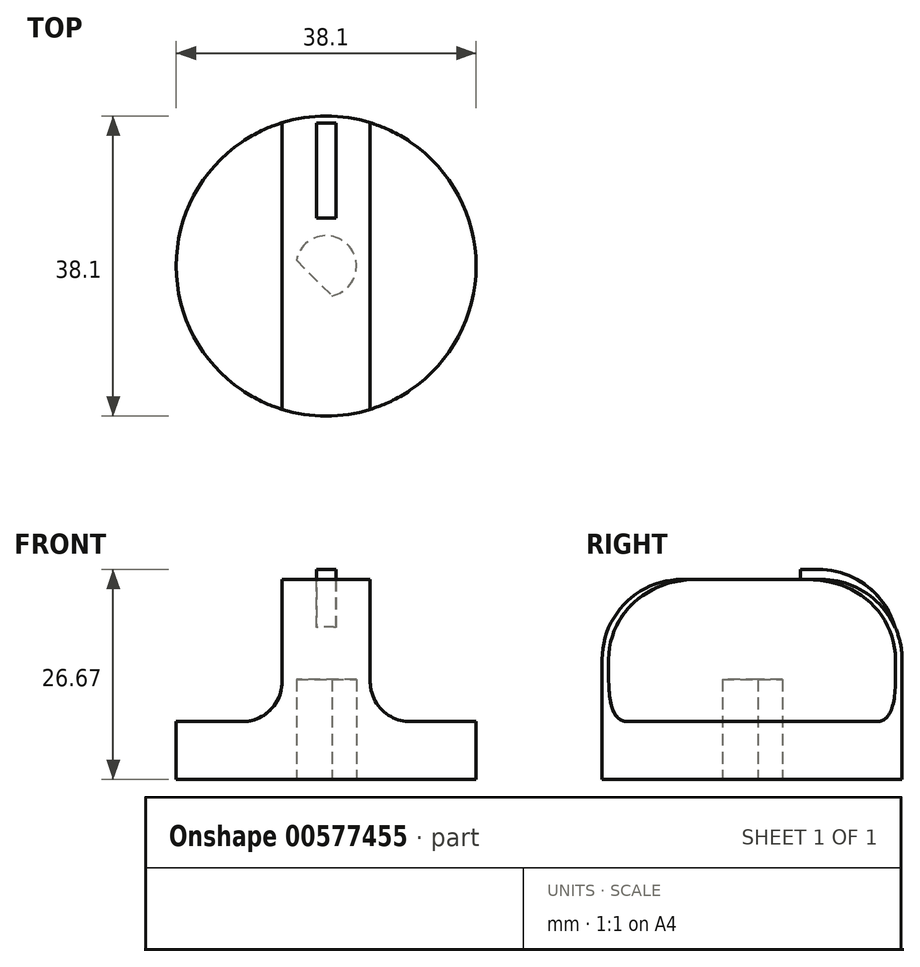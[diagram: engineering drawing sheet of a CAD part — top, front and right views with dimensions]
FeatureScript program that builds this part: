
annotation { "Feature Type Name" : "Feature", "Feature Type Description" : "" }
export const myFeature = defineFeature(function(context is Context, id is Id, definition is map)
    precondition{}
    {
        {
            var Q0;
            Q0=qCreatedBy(makeId("Top.planeOp"),FACE);
            var sketch = newSketch(context, id + "F0", { "sketchPlane" : qUnion([Q0])});
            skCircle(sketch, "E0", {"center": v(0, 0) * mm, "radius": 19.05 * mm});
            skCircle(sketch, "E1", {"center": v(0, 0) * mm, "radius": 3.5 * mm});
            skLineSegment(sketch, "E2", {"start": v(-3.4, 0.85) * mm, "end": v(0.85, -3.4) * mm});
            skSolve(sketch);
        }
        {
            var Q0;
            Q0=qCreatedBy(makeId("Top.planeOp"),FACE);
            var sketch = newSketch(context, id + "F1", { "sketchPlane" : qUnion([Q0])});
            skArc(sketch, "E3.0.0", {"start": v(0.85, -3.4) * mm, "mid": v(2.47, 2.47) * mm, "end": v(-3.4, 0.85) * mm});
            skLineSegment(sketch, "E3.0.1", {"start": v(-3.4, 0.85) * mm, "end": v(0.85, -3.4) * mm});
            skLineSegment(sketch, "E4.0", {"start": v(-3.78, 0.73) * mm, "end": v(0.73, -3.78) * mm});
            skArc(sketch, "E4.1", {"start": v(0.73, -3.78) * mm, "mid": v(2.72, 2.72) * mm, "end": v(-3.78, 0.73) * mm});
            skSolve(sketch);
        }
        {
            var Q0;
            {var subQ0=sQuery(id+"F0.wireOp",EDGE,"E2");Q0=makeQuery(id+"F0.imprint","IMPRINT",FACE,{"disambiguationData":[TD([[makeQuery(id+"F0.imprint","IMPRINT",EDGE,{"derivedFrom":subQ0}),-1.0]])]});}
            var Q1;
            {var subQ0=sQuery(id+"F0.wireOp",EDGE,"E2");Q1=makeQuery(id+"F0.imprint","IMPRINT",FACE,{"disambiguationData":[TD([[makeQuery(id+"F0.imprint","IMPRINT",EDGE,{"derivedFrom":subQ0}),1.0]])]});}
            var Q2;
            Q2=makeQuery(id+"F0.imprint","IMPRINT",FACE,{"disambiguationData":[TD([[makeQuery(id+"F0.imprint","IMPRINT",EDGE,{"derivedFrom":sQuery(id+"F0.wireOp",EDGE,"E0")}),1.0]])]});
            extrude(context, id + "F2", {"entities" : qUnion([Q0, Q1, Q2]), "depth" : 25.4 * mm, "offsetDistance" : 25.4 * mm});
        }
        {
            var Q0;
            Q0=qCreatedBy(makeId("Front.planeOp"),FACE);
            var sketch = newSketch(context, id + "F3", { "sketchPlane" : qUnion([Q0])});
            skLineSegment(sketch, "E5", {"start": v(-19.05, 0) * mm, "end": v(-19.05, 25.4) * mm, "construction": true});
            skLineSegment(sketch, "E6", {"start": v(19.05, 25.4) * mm, "end": v(19.05, 0) * mm, "construction": true});
            skLineSegment(sketch, "E7", {"start": v(-19.05, 7.34) * mm, "end": v(-5.6, 7.34) * mm});
            skLineSegment(sketch, "E8", {"start": v(-5.6, 7.34) * mm, "end": v(-5.6, 25.4) * mm});
            skLineSegment(sketch, "E9", {"start": v(-5.6, 25.4) * mm, "end": v(0, 25.4) * mm});
            skLineSegment(sketch, "E10.MirrorCS", {"start": v(5.6, 7.34) * mm, "end": v(5.6, 25.4) * mm});
            skLineSegment(sketch, "E11.MirrorCS", {"start": v(19.05, 7.34) * mm, "end": v(5.6, 7.34) * mm});
            skLineSegment(sketch, "E12.MirrorCS", {"start": v(5.6, 25.4) * mm, "end": v(0, 25.4) * mm});
            skLineSegment(sketch, "E13", {"start": v(-19.05, 7.34) * mm, "end": v(-19.05, 25.4) * mm});
            skLineSegment(sketch, "E14", {"start": v(-19.05, 25.4) * mm, "end": v(19.05, 25.4) * mm});
            skLineSegment(sketch, "E15", {"start": v(19.05, 25.4) * mm, "end": v(19.05, 7.34) * mm});
            skSolve(sketch);
        }
        {
            var Q0;
            Q0 = qSketchRegion(id + "F3", true);
            extrude(context, id + "F4", {"entities" : qUnion([Q0]), "operationType" : NewBodyOperationType.REMOVE, "endBound" : BoundingType.SYMMETRIC, "depth" : 76.2 * mm, "offsetDistance" : 25.4 * mm});
        }
        {
            var Q0;
            Q0=makeQuery(id+"F1.imprint","IMPRINT",FACE,{"disambiguationData":[TD([[makeQuery(id+"F1.imprint","IMPRINT",EDGE,{"derivedFrom":sQuery(id+"F1.wireOp",EDGE,"E3.0.0")}),1.0]])]});
            var Q1;
            Q1=makeQuery(id+"F1.imprint","IMPRINT",FACE,{"disambiguationData":[TD([[makeQuery(id+"F1.imprint","IMPRINT",EDGE,{"derivedFrom":sQuery(id+"F1.wireOp",EDGE,"E3.0.0")}),-1.0]])]});
            extrude(context, id + "F5", {"entities" : qUnion([Q0, Q1]), "operationType" : NewBodyOperationType.REMOVE, "depth" : 12.7 * mm, "offsetDistance" : 25.4 * mm});
        }
        {
            var Q0;
            Q0=makeQuery(id+"F4.boolean.opBoolean","COPY",EDGE,{"derivedFrom":makeQuery(id+"F4.opExtrude","SWEPT_EDGE",EDGE,{"disambiguationData":[OSD([sQuery(id+"F3.wireOp",EDGE,"E7"),sQuery(id+"F3.wireOp",EDGE,"E8")])]})});
            var Q1;
            Q1=makeQuery(id+"F4.boolean.opBoolean","COPY",EDGE,{"derivedFrom":makeQuery(id+"F4.opExtrude","SWEPT_EDGE",EDGE,{"disambiguationData":[OSD([sQuery(id+"F3.wireOp",EDGE,"E10.MirrorCS"),sQuery(id+"F3.wireOp",EDGE,"E11.MirrorCS")])]})});
            fillet(context, id + "F6", {"entities" : qUnion([Q0, Q1]), "radius" : 5.08 * mm, "tangentPropagation" : true, "allowEdgeOverflow" : false});
        }
        {
            var Q0;
            Q0=qCreatedBy(makeId("Top.planeOp"),FACE);
            var sketch = newSketch(context, id + "F7", { "sketchPlane" : qUnion([Q0])});
            skLineSegment(sketch, "E16.bottom", {"start": v(1.24, 6.12) * mm, "end": v(-1.24, 6.12) * mm});
            skLineSegment(sketch, "E16.top", {"start": v(1.24, 18.16) * mm, "end": v(-1.24, 18.16) * mm});
            skLineSegment(sketch, "E16.left", {"start": v(1.24, 6.12) * mm, "end": v(1.24, 18.16) * mm});
            skLineSegment(sketch, "E16.right", {"start": v(-1.24, 6.12) * mm, "end": v(-1.24, 18.16) * mm});
            skPoint(sketch, "E16.middle", {"position": v(0, 12.14) * mm});
            skSolve(sketch);
        }
        {
            var Q0;
            Q0 = qSketchRegion(id + "F7", true);
            extrude(context, id + "F8", {"entities" : qUnion([Q0]), "operationType" : NewBodyOperationType.ADD, "depth" : 26.67 * mm, "offsetDistance" : 25.4 * mm});
        }
        {
            var Q0;
            Q0=makeQuery(id+"F4.boolean.opBoolean","SPLIT",EDGE,{"disambiguationData":[OD(0.0)],"derivedFrom":makeQuery(id+"F2.opExtrude","CAP_EDGE",EDGE,{"disambiguationData":[OSD([sQuery(id+"F0.wireOp",EDGE,"E0")])],"isStart":false})});
            var Q1;
            Q1=makeQuery(id+"F4.boolean.opBoolean","SPLIT",EDGE,{"disambiguationData":[OD(1.0)],"derivedFrom":makeQuery(id+"F2.opExtrude","CAP_EDGE",EDGE,{"disambiguationData":[OSD([sQuery(id+"F0.wireOp",EDGE,"E0")])],"isStart":false})});
            fillet(context, id + "F9", {"entities" : qUnion([Q0, Q1]), "radius" : 10.16 * mm, "tangentPropagation" : true, "allowEdgeOverflow" : false});
        }
        {
            var Q0;
            Q0=makeQuery(id+"F8.opExtrude","CAP_EDGE",EDGE,{"disambiguationData":[OSD([sQuery(id+"F7.wireOp",EDGE,"E16.top")])],"isStart":false});
            fillet(context, id + "F10", {"entities" : qUnion([Q0]), "radius" : 10.16 * mm, "tangentPropagation" : true, "allowEdgeOverflow" : false});
        }
    });
